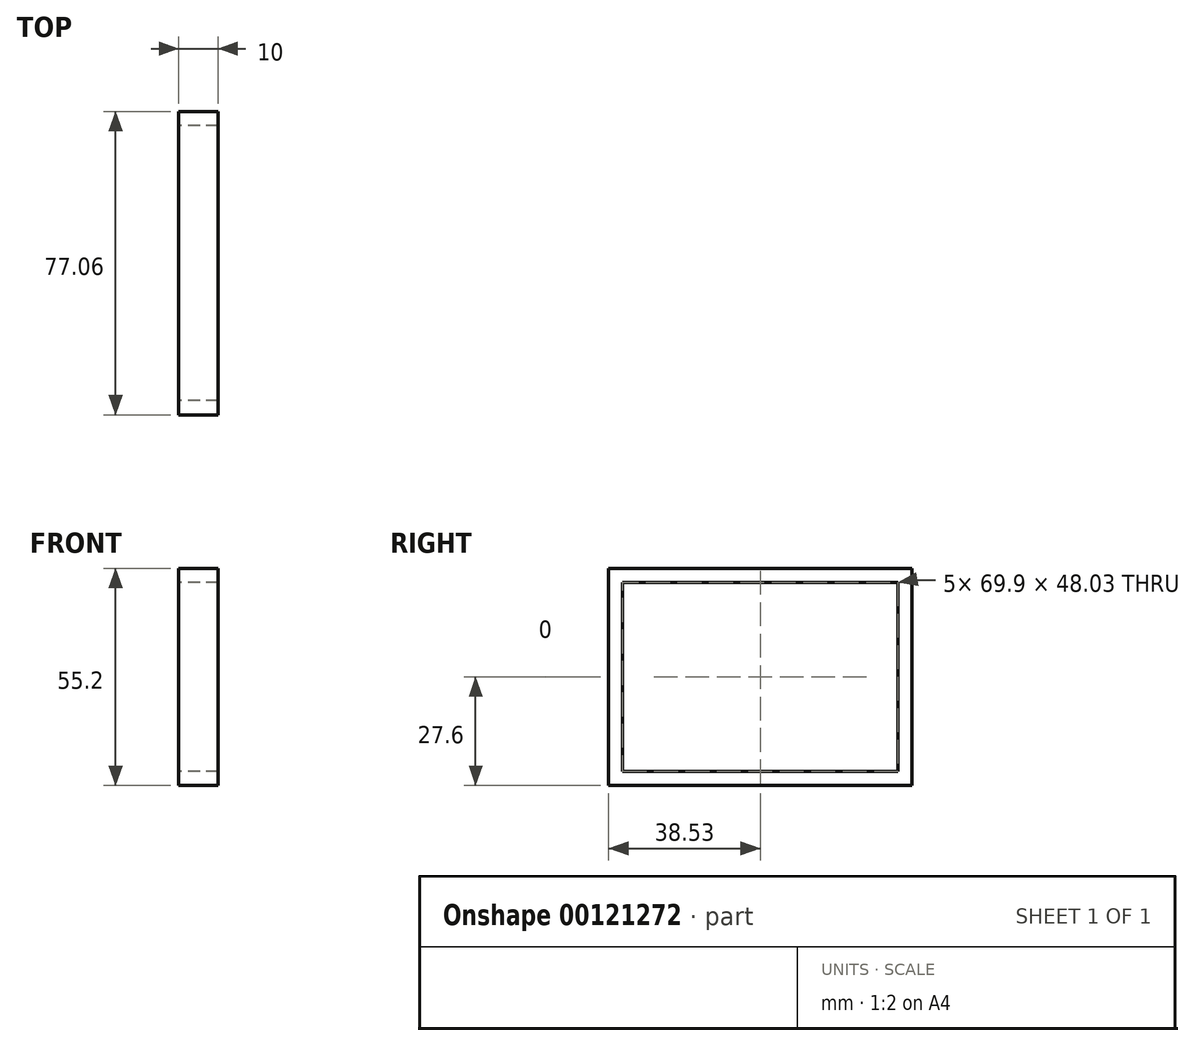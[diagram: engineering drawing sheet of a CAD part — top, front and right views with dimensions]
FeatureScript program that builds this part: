
annotation { "Feature Type Name" : "Feature", "Feature Type Description" : "" }
export const myFeature = defineFeature(function(context is Context, id is Id, definition is map)
    precondition{}
    {
        {
            var Q0;
            Q0=qCreatedBy(makeId("Right.planeOp"),FACE);
            var sketch = newSketch(context, id + "F0", { "sketchPlane" : qUnion([Q0])});
            skLineSegment(sketch, "E0.bottom", {"start": v(38.53, 27.6) * mm, "end": v(-38.53, 27.6) * mm});
            skLineSegment(sketch, "E0.top", {"start": v(38.53, -27.6) * mm, "end": v(-38.53, -27.6) * mm});
            skLineSegment(sketch, "E0.left", {"start": v(38.53, 27.6) * mm, "end": v(38.53, -27.6) * mm});
            skLineSegment(sketch, "E0.right", {"start": v(-38.53, 27.6) * mm, "end": v(-38.53, -27.6) * mm});
            skPoint(sketch, "E0.middle", {"position": v(0, 0) * mm});
            skLineSegment(sketch, "E1.0", {"start": v(34.95, 24.01) * mm, "end": v(-34.95, 24.01) * mm});
            skLineSegment(sketch, "E1.1", {"start": v(34.95, 24.01) * mm, "end": v(34.95, -24.01) * mm});
            skLineSegment(sketch, "E1.2", {"start": v(34.95, -24.01) * mm, "end": v(-34.95, -24.01) * mm});
            skLineSegment(sketch, "E1.3", {"start": v(-34.95, 24.01) * mm, "end": v(-34.95, -24.01) * mm});
            skSolve(sketch);
        }
        {
            var Q0;
            Q0=makeQuery(id+"F0.imprint","IMPRINT",FACE,{"disambiguationData":[TD([[makeQuery(id+"F0.imprint","IMPRINT",EDGE,{"derivedFrom":sQuery(id+"F0.wireOp",EDGE,"E0.bottom")}),1.0]])]});
            extrude(context, id + "F1", {"entities" : qUnion([Q0]), "depth" : 10 * mm});
        }
    });
